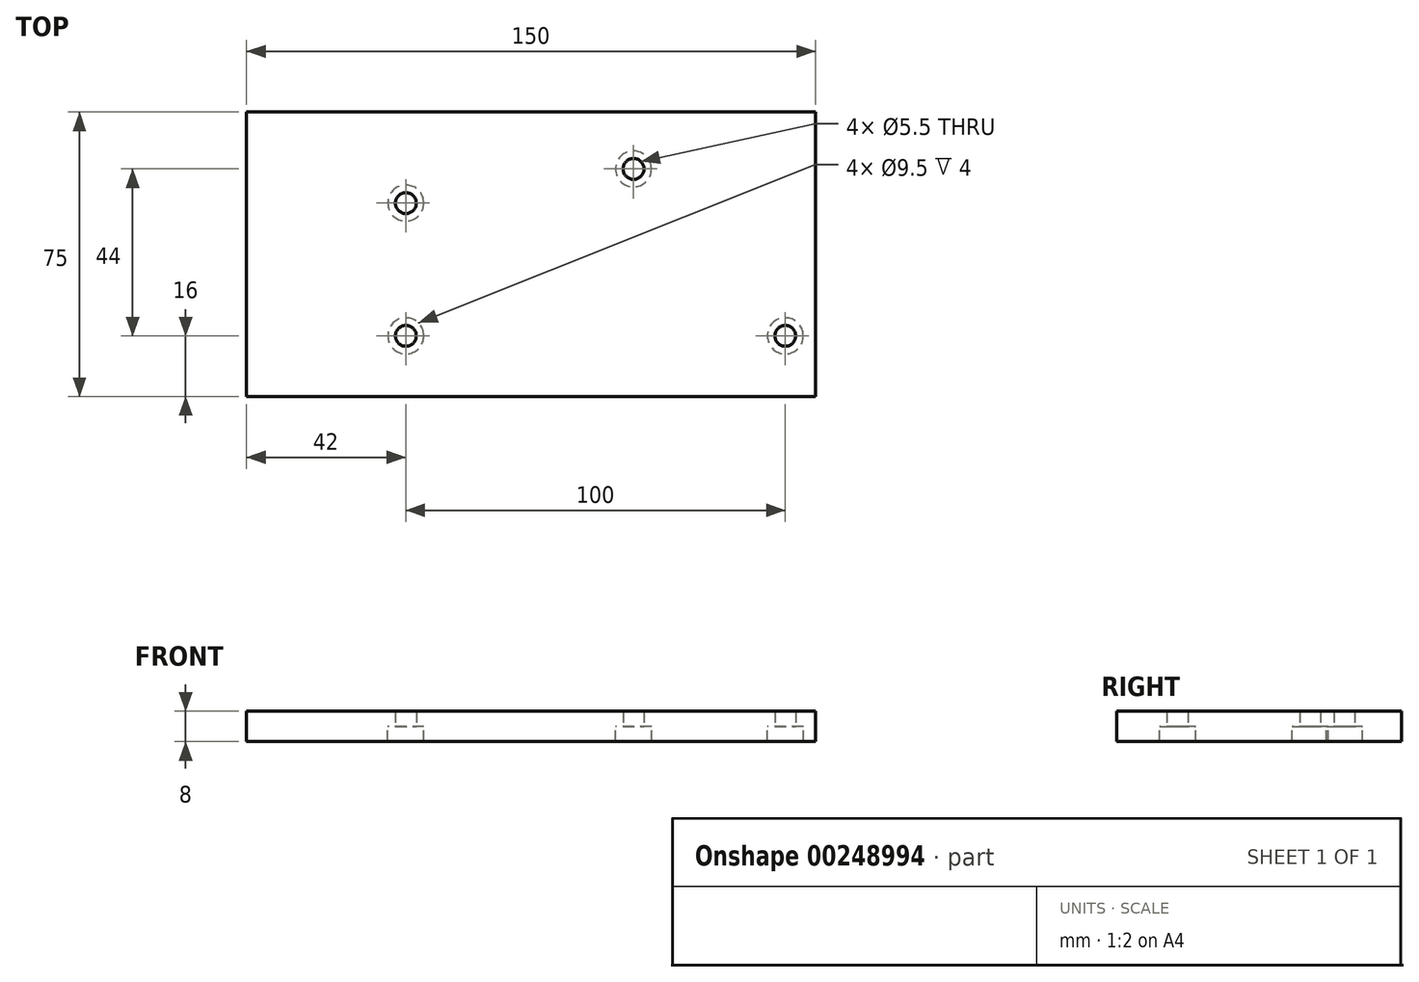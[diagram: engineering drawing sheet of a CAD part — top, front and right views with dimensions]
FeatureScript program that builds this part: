
annotation { "Feature Type Name" : "Feature", "Feature Type Description" : "" }
export const myFeature = defineFeature(function(context is Context, id is Id, definition is map)
    precondition{}
    {
        {
            var Q0;
            Q0=qCreatedBy(makeId("Top.planeOp"),FACE);
            var sketch = newSketch(context, id + "F0", { "sketchPlane" : qUnion([Q0])});
            skLineSegment(sketch, "E0.bottom", {"start": v(75, -37.5) * mm, "end": v(-75, -37.5) * mm});
            skLineSegment(sketch, "E0.top", {"start": v(75, 37.5) * mm, "end": v(-75, 37.5) * mm});
            skLineSegment(sketch, "E0.left", {"start": v(75, -37.5) * mm, "end": v(75, 37.5) * mm});
            skLineSegment(sketch, "E0.right", {"start": v(-75, -37.5) * mm, "end": v(-75, 37.5) * mm});
            skPoint(sketch, "E0.middle", {"position": v(0, 0) * mm});
            skCircle(sketch, "E1", {"center": v(-33, 13.5) * mm, "radius": 2.75 * mm});
            skCircle(sketch, "E2", {"center": v(27, 22.5) * mm, "radius": 2.75 * mm});
            skCircle(sketch, "E3", {"center": v(-33, -21.5) * mm, "radius": 2.75 * mm});
            skCircle(sketch, "E4", {"center": v(67, -21.5) * mm, "radius": 2.75 * mm});
            skSolve(sketch);
        }
        {
            var Q0;
            Q0=makeQuery(id+"F0.imprint","IMPRINT",FACE,{"disambiguationData":[TD([[makeQuery(id+"F0.imprint","IMPRINT",EDGE,{"derivedFrom":sQuery(id+"F0.wireOp",EDGE,"E0.bottom")}),-1.0]])]});
            extrude(context, id + "F1", {"entities" : qUnion([Q0]), "endBound" : BoundingType.SYMMETRIC, "depth" : 8 * mm});
        }
        {
            var Q0;
            Q0=sQuery(id+"F0.wireOp",VERTEX,"E2.center");
            var Q1;
            Q1=sQuery(id+"F0.wireOp",VERTEX,"E4.center");
            var Q2;
            Q2=sQuery(id+"F0.wireOp",VERTEX,"E3.center");
            var Q3;
            Q3=sQuery(id+"F0.wireOp",VERTEX,"E1.center");
            var Q4;
            Q4=makeQuery(id+"F1.opExtrude","SWEPT_BODY",BODY,{"disambiguationData":[OSD([sQuery(id+"F0.wireOp",EDGE,"E0.bottom"),sQuery(id+"F0.wireOp",EDGE,"E0.top"),sQuery(id+"F0.wireOp",EDGE,"E0.left"),sQuery(id+"F0.wireOp",EDGE,"E0.right"),sQuery(id+"F0.wireOp",EDGE,"E1"),sQuery(id+"F0.wireOp",EDGE,"E2"),sQuery(id+"F0.wireOp",EDGE,"E3"),sQuery(id+"F0.wireOp",EDGE,"E4")])]});
            hole(context, id + "F2", {"style" : HoleStyle.C_BORE, "endStyle" : HoleEndStyle.BLIND, "holeDiameter" : 5.5 * mm, "cBoreDiameter" : 9.5 * mm, "cBoreDepth" : 5 * mm, "holeDepth" : 8 * mm, "tappedDepth" : 12 * mm, "tapClearance" : 3, "startFromSketch" : true, "locations" : qUnion([Q0, Q1, Q2, Q3]), "scope" : qUnion([Q4])});
        }
    });
